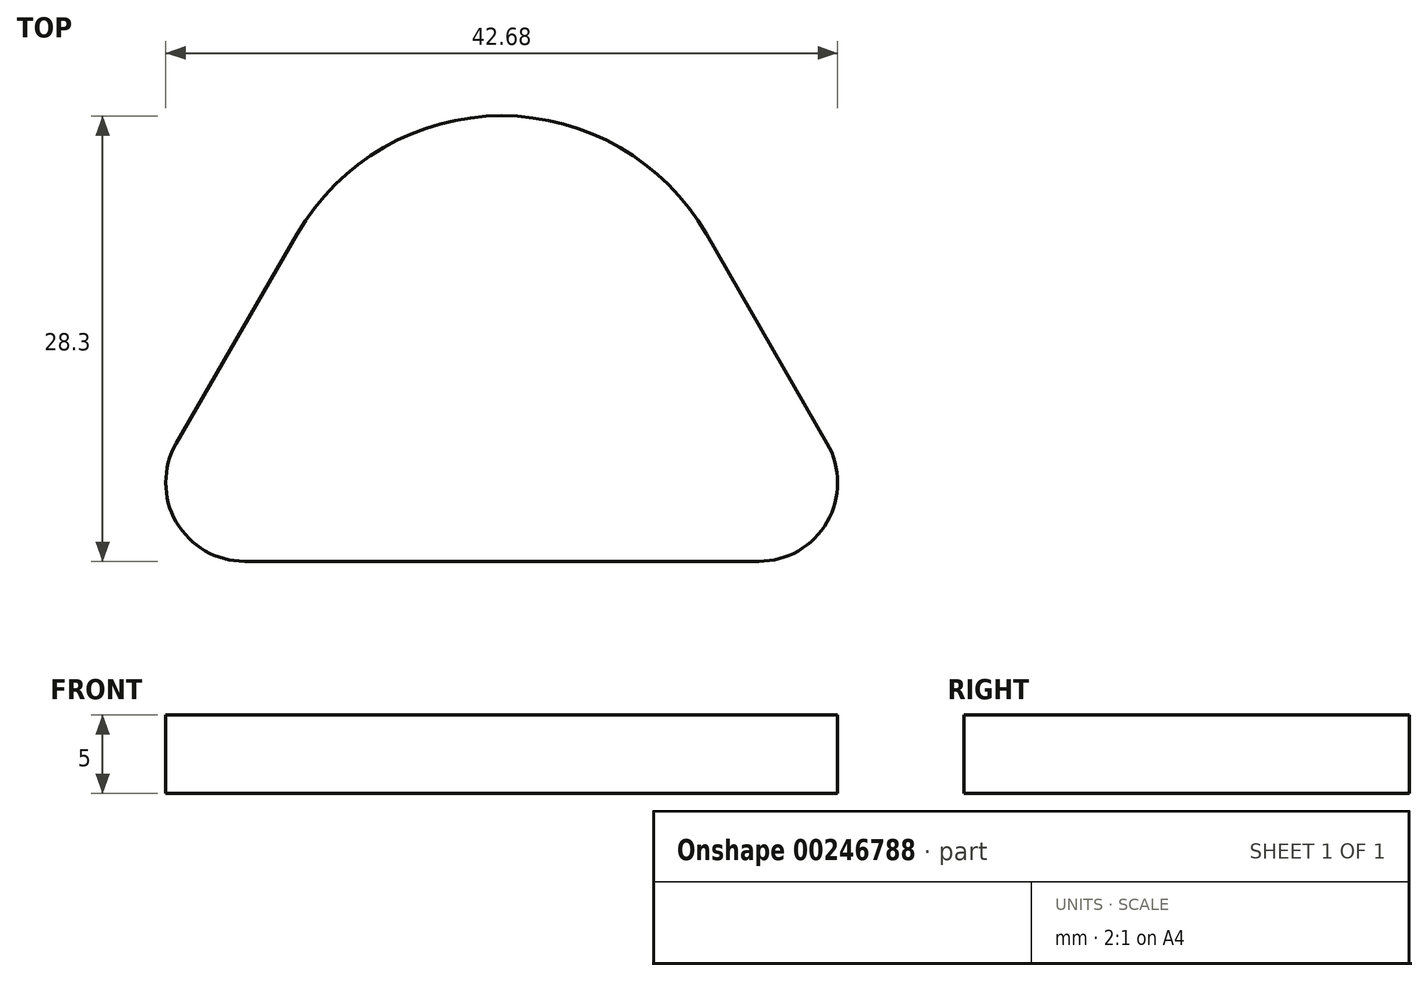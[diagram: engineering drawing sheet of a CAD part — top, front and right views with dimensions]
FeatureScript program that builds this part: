
annotation { "Feature Type Name" : "Feature", "Feature Type Description" : "" }
export const myFeature = defineFeature(function(context is Context, id is Id, definition is map)
    precondition{}
    {
        {
            var Q0;
            Q0=qCreatedBy(makeId("Top.planeOp"),FACE);
            var sketch = newSketch(context, id + "F0", { "sketchPlane" : qUnion([Q0])});
            skCircle(sketch, "E0.cCircle", {"center": v(37.42, -21.52) * mm, "radius": 14.43 * mm, "construction": true});
            skLineSegment(sketch, "E0.0", {"start": v(62.42, -35.96) * mm, "end": v(12.42, -35.96) * mm});
            skLineSegment(sketch, "E0.1", {"start": v(12.42, -35.96) * mm, "end": v(37.42, 7.34) * mm});
            skLineSegment(sketch, "E0.2", {"start": v(37.42, 7.34) * mm, "end": v(62.42, -35.96) * mm});
            skPoint(sketch, "E0.0.midPoint", {"position": v(37.42, -35.96) * mm});
            skSolve(sketch);
        }
        {
            var Q0;
            Q0=makeQuery(id+"F0.imprint","IMPRINT",FACE,{"disambiguationData":[TD([[makeQuery(id+"F0.imprint","IMPRINT",EDGE,{"derivedFrom":sQuery(id+"F0.wireOp",EDGE,"E0.0")}),-1.0]])]});
            extrude(context, id + "F1", {"entities" : qUnion([Q0]), "depth" : 5 * mm});
        }
        {
            var Q0;
            Q0=makeQuery(id+"F1.opExtrude","SWEPT_EDGE",EDGE,{"disambiguationData":[OSD([sQuery(id+"F0.wireOp",EDGE,"E0.0"),sQuery(id+"F0.wireOp",EDGE,"E0.2")])]});
            var Q1;
            Q1=makeQuery(id+"F1.opExtrude","SWEPT_EDGE",EDGE,{"disambiguationData":[OSD([sQuery(id+"F0.wireOp",EDGE,"E0.0"),sQuery(id+"F0.wireOp",EDGE,"E0.1")])]});
            fillet(context, id + "F2", {"entities" : qUnion([Q0, Q1]), "radius" : 5 * mm, "tangentPropagation" : true, "allowEdgeOverflow" : false});
        }
        {
            var Q0;
            Q0=makeQuery(id+"F1.opExtrude","SWEPT_EDGE",EDGE,{"disambiguationData":[OSD([sQuery(id+"F0.wireOp",EDGE,"E0.1"),sQuery(id+"F0.wireOp",EDGE,"E0.2")])]});
            fillet(context, id + "F3", {"entities" : qUnion([Q0]), "radius" : 15 * mm, "tangentPropagation" : true, "allowEdgeOverflow" : false});
        }
    });
